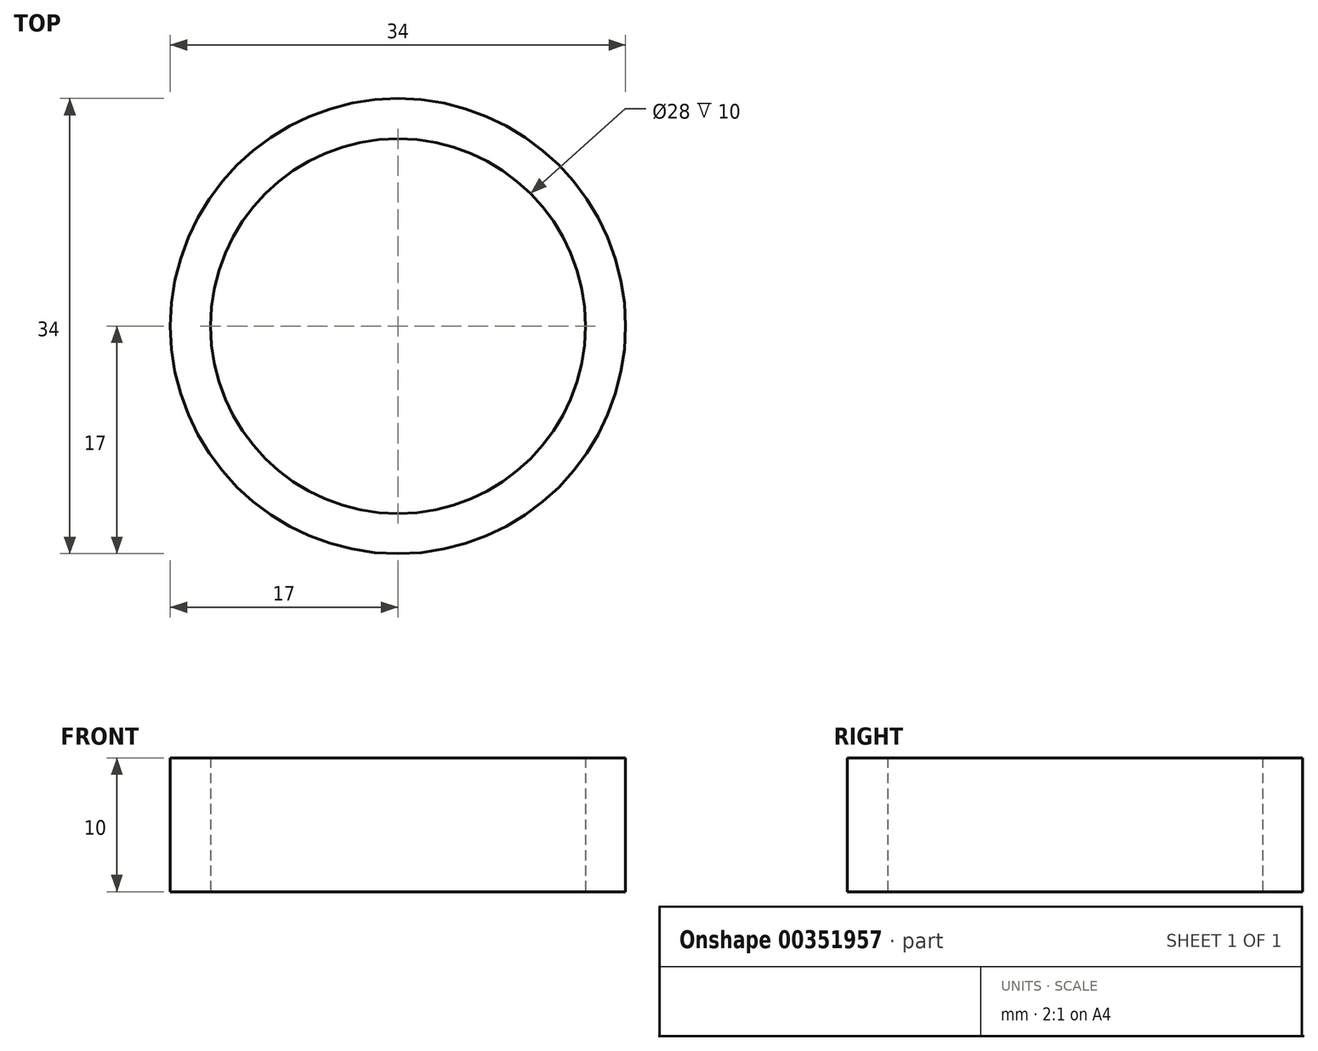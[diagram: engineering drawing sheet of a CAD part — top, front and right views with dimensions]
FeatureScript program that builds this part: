
annotation { "Feature Type Name" : "Feature", "Feature Type Description" : "" }
export const myFeature = defineFeature(function(context is Context, id is Id, definition is map)
    precondition{}
    {
        {
            var Q0;
            Q0=qCreatedBy(makeId("Top.planeOp"),FACE);
            var sketch = newSketch(context, id + "F0", { "sketchPlane" : qUnion([Q0])});
            skCircle(sketch, "E0", {"center": v(0, 0) * mm, "radius": 14 * mm});
            skCircle(sketch, "E1", {"center": v(0, 0) * mm, "radius": 17 * mm});
            skSolve(sketch);
        }
        {
            var Q0;
            Q0=makeQuery(id+"F0.imprint","IMPRINT",FACE,{"disambiguationData":[TD([[makeQuery(id+"F0.imprint","IMPRINT",EDGE,{"derivedFrom":sQuery(id+"F0.wireOp",EDGE,"E0")}),-1.0]])]});
            extrude(context, id + "F1", {"entities" : qUnion([Q0]), "depth" : 10 * mm});
        }
    });
